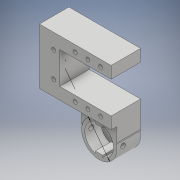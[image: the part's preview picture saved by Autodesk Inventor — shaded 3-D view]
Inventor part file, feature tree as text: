
AUTODESK INVENTOR PART (.ipt)
format: ipt  version: 2018 (Build 220112000, 112)  size: 287,232 bytes
history: native  units: mm
features: sketch x11, extrude x10, other x2, fillet x1, hole x1
ambient origin geometry x8: Origin, YZ Plane, XZ Plane, XY Plane, X Axis, Y Axis, Z Axis, Center Point
bodies: Solide1 (feature_tree)
feature tree (25):
  other  "Annotations"
  extrude  "Extrusion1"  Depth=22.0mm
  extrude  "Extrusion2"  Depth=19.0mm
  extrude  "Extrusion3"  Depth=5.0mm TaperAngle=0.0deg
  extrude  "Extrusion5"  Depth=22.0mm
  extrude  "Extrusion14"  Depth=10.0mm TaperAngle=0.0deg
  extrude  "Extrusion15"  Depth=10.0mm TaperAngle=0.0deg
  extrude  "Extrusion13"  TaperAngle=0.0deg  [1 undecoded]
  extrude  "Extrusion17"  Depth=9.0mm
  fillet  "Congé2"  Radius=9.0mm
  extrude  "Extrusion18"  Depth=3.0mm
  sketch  "Esquisse1"
  sketch  "Esquisse2"
  sketch  "Esquisse3"
  sketch  "Esquisse5"
  sketch  "Esquisse18"
  sketch  "Esquisse19"
  sketch  "Esquisse21"
  sketch  "Esquisse22"
  hole  "Perçage3"  [1 undecoded]
  sketch  "Esquisse14"
  sketch  "Esquisse15"
  sketch  "Esquisse17"
  other  "Cote de diamètre 1"
  extrude  "Extrusion11"  Depth=30.0mm TaperAngle=0.0deg
note: 2 required parameter values undecoded (feature->parameter linkage not recoverable at this tier; creation-order binding heuristic only, values carry confidence <= 0.55)
